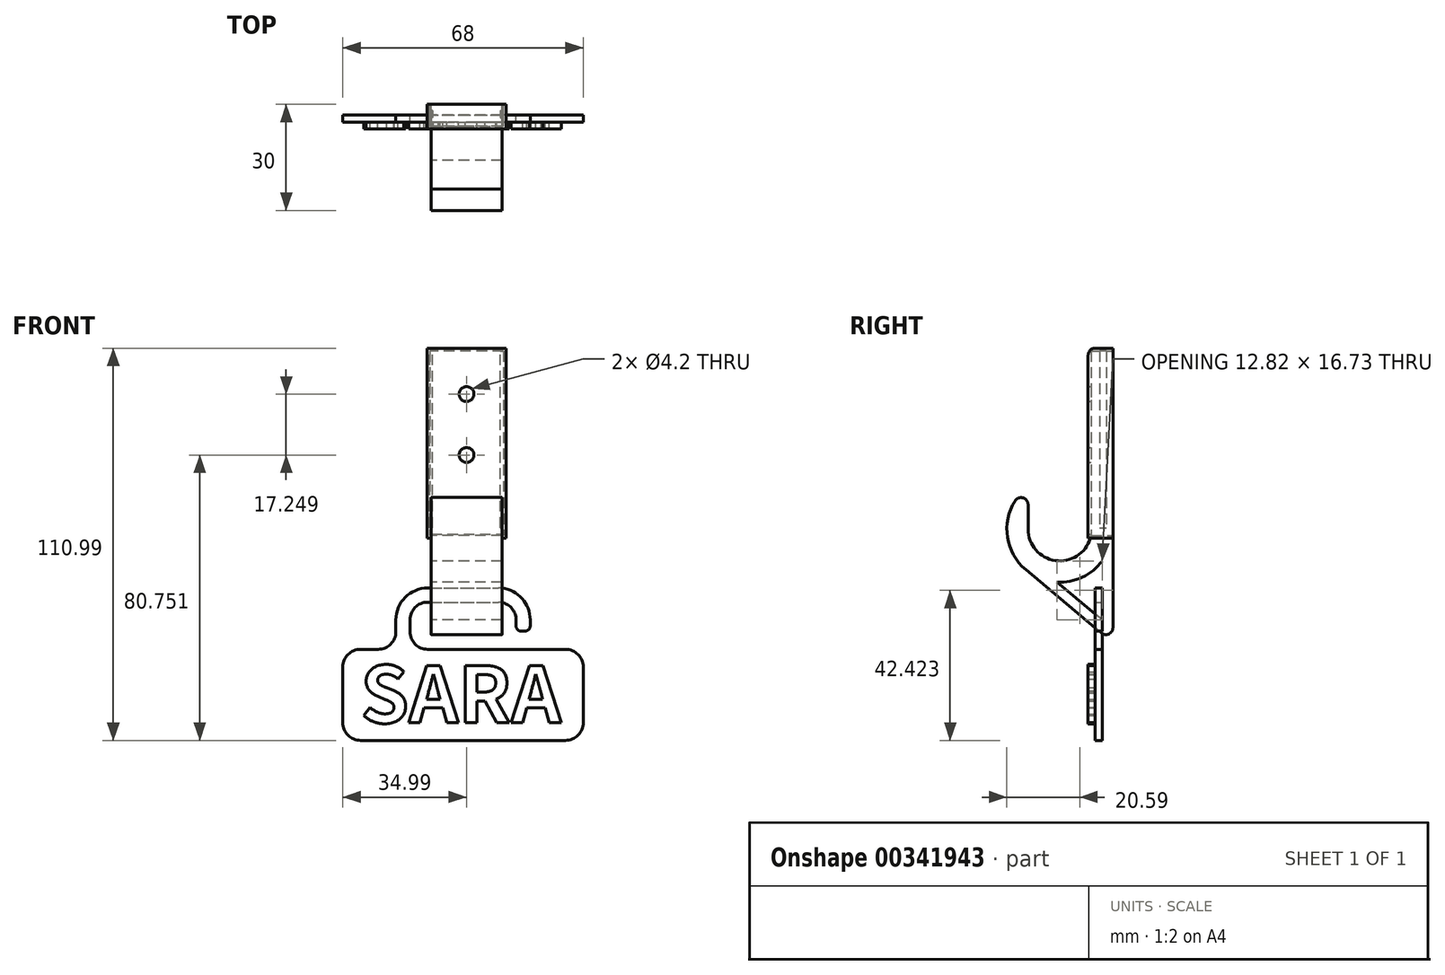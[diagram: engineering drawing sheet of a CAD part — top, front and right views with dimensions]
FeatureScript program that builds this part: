
annotation { "Feature Type Name" : "Feature", "Feature Type Description" : "" }
export const myFeature = defineFeature(function(context is Context, id is Id, definition is map)
    precondition{}
    {
        {
            var Q0;
            Q0=qCreatedBy(makeId("Right.planeOp"),FACE);
            var sketch = newSketch(context, id + "F0", { "sketchPlane" : qUnion([Q0])});
            skLineSegment(sketch, "E0.bottom", {"start": v(3, -25) * mm, "end": v(-3, -25) * mm});
            skLineSegment(sketch, "E0.top", {"start": v(3, 25) * mm, "end": v(-1, 25) * mm});
            skLineSegment(sketch, "E0.left", {"start": v(3, -25) * mm, "end": v(3, 25) * mm});
            skLineSegment(sketch, "E0.right", {"start": v(-3, -25) * mm, "end": v(-3, 23) * mm});
            skPoint(sketch, "E0.middle", {"position": v(0, 0) * mm});
            skArc(sketch, "E1", {"start": v(-24.7, -17) * mm, "mid": v(-9.28, -39.75) * mm, "end": v(-3, -13) * mm});
            skCircle(sketch, "E2", {"center": v(-12, -25) * mm, "radius": 9 * mm});
            skLineSegment(sketch, "E3", {"start": v(-21, -18.07) * mm, "end": v(-21, -25) * mm});
            skPoint(sketch, "E4.visualSharp", {"position": v(-21, -13) * mm});
            skArc(sketch, "E4.filletArc", {"start": v(-21, -18.07) * mm, "mid": v(-22.45, -16.15) * mm, "end": v(-24.7, -17) * mm});
            skLineSegment(sketch, "E5", {"start": v(3, -25) * mm, "end": v(3, -52.88) * mm});
            skLineSegment(sketch, "E6", {"start": v(-0.29, -54.41) * mm, "end": v(-21.64, -36.5) * mm});
            skPoint(sketch, "E7.visualSharp", {"position": v(3, -57.17) * mm});
            skArc(sketch, "E7.filletArc", {"start": v(-0.29, -54.41) * mm, "mid": v(1.85, -54.7) * mm, "end": v(3, -52.88) * mm});
            skPoint(sketch, "E8.visualSharp", {"position": v(-3, 25) * mm});
            skArc(sketch, "E8.filletArc", {"start": v(-1, 25) * mm, "mid": v(-2.41, 24.41) * mm, "end": v(-3, 23) * mm});
            skLineSegment(sketch, "E9.0", {"start": v(0, -50.73) * mm, "end": v(-12.82, -39.98) * mm});
            skLineSegment(sketch, "E9.1", {"start": v(0, -34) * mm, "end": v(0, -50.73) * mm});
            skSolve(sketch);
        }
        {
            var Q0;
            {var subQ1=sQuery(id+"F0.wireOp",EDGE,"E5");Q0=makeQuery(id+"F0.imprint","IMPRINT",FACE,{"disambiguationData":[TD([[makeQuery(id+"F0.imprint","IMPRINT",EDGE,{"derivedFrom":subQ1}),-1.0]])]});}
            var Q1;
            {var subQ5=sQuery(id+"F0.wireOp",EDGE,"E0.bottom");Q1=makeQuery(id+"F0.imprint","IMPRINT",FACE,{"disambiguationData":[TD([[makeQuery(id+"F0.imprint","IMPRINT",EDGE,{"derivedFrom":subQ5}),1.0]])]});}
            var Q2;
            {var subQ0=sQuery(id+"F0.wireOp",EDGE,"E0.bottom");Q2=makeQuery(id+"F0.imprint","IMPRINT",FACE,{"disambiguationData":[TD([[makeQuery(id+"F0.imprint","IMPRINT",EDGE,{"derivedFrom":subQ0}),-1.0]])]});}
            var Q3;
            Q3=makeQuery(id+"F0.imprint","IMPRINT",FACE,{"disambiguationData":[TD([[makeQuery(id+"F0.imprint","IMPRINT",EDGE,{"derivedFrom":sQuery(id+"F0.wireOp",EDGE,"E0.top")}),1.0]])]});
            extrude(context, id + "F1", {"entities" : qUnion([Q0, Q1, Q2, Q3]), "depth" : 20 * mm});
        }
        {
            var Q0;
            Q0=makeQuery(id+"F1.opExtrude","SWEPT_FACE",FACE,{"disambiguationData":[OSD([sQuery(id+"F0.wireOp",EDGE,"E0.right")])]});
            var sketch = newSketch(context, id + "F2", { "sketchPlane" : qUnion([Q0])});
            skPoint(sketch, "E10", {"position": v(10, 13.21) * mm});
            skPoint(sketch, "E10.positionSnap0", {"position": v(10, 23) * mm});
            skPoint(sketch, "E11", {"position": v(10, -4.04) * mm});
            skPoint(sketch, "E12.endSnap0", {"position": v(10, -25) * mm});
            skSolve(sketch);
        }
        {
            var Q0;
            Q0=sQuery(id+"F2.wireOp",VERTEX,"E10");
            var Q1;
            Q1=sQuery(id+"F2.wireOp",VERTEX,"E11");
            var Q2;
            Q2=makeQuery(id+"F1.opExtrude","SWEPT_BODY",BODY,{"disambiguationData":[OSD([sQuery(id+"F0.wireOp",EDGE,"E0.top"),sQuery(id+"F0.wireOp",EDGE,"E0.left"),sQuery(id+"F0.wireOp",EDGE,"E0.right"),sQuery(id+"F0.wireOp",EDGE,"E1"),sQuery(id+"F0.wireOp",EDGE,"E2"),sQuery(id+"F0.wireOp",EDGE,"E3"),sQuery(id+"F0.wireOp",EDGE,"E4.filletArc"),sQuery(id+"F0.wireOp",EDGE,"E5"),sQuery(id+"F0.wireOp",EDGE,"E6"),sQuery(id+"F0.wireOp",EDGE,"E7.filletArc"),sQuery(id+"F0.wireOp",EDGE,"E8.filletArc"),sQuery(id+"F0.wireOp",EDGE,"E9.0"),sQuery(id+"F0.wireOp",EDGE,"E9.1")])]});
            hole(context, id + "F3", {"style" : HoleStyle.C_SINK, "endStyle" : HoleEndStyle.BLIND, "standardTappedOrClearance" : lookupTablePath({ "standard" : "ISO", "engagement" : "75%", "pitch" : "0.8 mm", "size" : "M5", "type" : "Tapped" }), "standardBlindInLast" : lookupTablePath({ "standard" : "ISO", "engagement" : "75%", "pitch" : "0.8 mm", "size" : "M5", "type" : "Tapped" }), "holeDiameter" : 4.2 * mm, "cSinkDiameter" : 11.2 * mm, "cSinkAngle" : 90 * degree, "showTappedDepth" : true, "holeDepth" : 14.4 * mm, "isTappedThrough" : true, "tappedDepth" : 12 * mm, "tapClearance" : 3, "startFromSketch" : true, "locations" : qUnion([Q0, Q1]), "scope" : qUnion([Q2]), "majorDiameter" : 5 * mm});
        }
        {
            var Q0;
            Q0=makeQuery(id+"F1.opExtrude","SWEPT_FACE",FACE,{"disambiguationData":[OSD([sQuery(id+"F0.wireOp",EDGE,"E0.left"),sQuery(id+"F0.wireOp",EDGE,"E5")])]});
            var sketch = newSketch(context, id + "F4", { "sketchPlane" : qUnion([Q0])});
            skLineSegment(sketch, "E13.bottom", {"start": v(-20, 25) * mm, "end": v(0, 25) * mm});
            skLineSegment(sketch, "E13.top", {"start": v(-20, -26.42) * mm, "end": v(0, -26.42) * mm});
            skLineSegment(sketch, "E13.left", {"start": v(-20, 25) * mm, "end": v(-20, -26.42) * mm});
            skLineSegment(sketch, "E13.right", {"start": v(0, 25) * mm, "end": v(0, -26.42) * mm});
            skLineSegment(sketch, "E14.bottom", {"start": v(-21.2, 26.2) * mm, "end": v(1.2, 26.2) * mm});
            skLineSegment(sketch, "E14.top", {"start": v(-21.2, -27.62) * mm, "end": v(1.2, -27.62) * mm});
            skLineSegment(sketch, "E14.left", {"start": v(-21.2, 26.2) * mm, "end": v(-21.2, -27.62) * mm});
            skLineSegment(sketch, "E14.right", {"start": v(1.2, 26.2) * mm, "end": v(1.2, -27.62) * mm});
            skLineSegment(sketch, "E15.bottom", {"start": v(-20.4, 25.4) * mm, "end": v(0.4, 25.4) * mm});
            skLineSegment(sketch, "E15.top", {"start": v(-20.4, -26.82) * mm, "end": v(0.4, -26.82) * mm});
            skLineSegment(sketch, "E15.left", {"start": v(-20.4, 25.4) * mm, "end": v(-20.4, -26.82) * mm});
            skLineSegment(sketch, "E15.right", {"start": v(0.4, 25.4) * mm, "end": v(0.4, -26.82) * mm});
            skSolve(sketch);
        }
        {
            var Q0;
            Q0=makeQuery(id+"F4.imprint","IMPRINT",FACE,{"disambiguationData":[TD([[makeQuery(id+"F4.imprint","IMPRINT",EDGE,{"derivedFrom":sQuery(id+"F4.wireOp",EDGE,"E13.bottom")}),-1.0]])]});
            var Q1;
            Q1=makeQuery(id+"F4.imprint","IMPRINT",FACE,{"disambiguationData":[TD([[makeQuery(id+"F4.imprint","IMPRINT",EDGE,{"derivedFrom":sQuery(id+"F4.wireOp",EDGE,"E13.bottom")}),1.0]])]});
            var Q2;
            Q2=makeQuery(id+"F4.imprint","IMPRINT",FACE,{"disambiguationData":[TD([[makeQuery(id+"F4.imprint","IMPRINT",EDGE,{"derivedFrom":sQuery(id+"F4.wireOp",EDGE,"E14.bottom")}),-1.0]])]});
            var Q3;
            Q3=makeQuery(id+"F4.imprint","IMPRINT",FACE,{"disambiguationData":[TD([[makeQuery(id+"F4.imprint","IMPRINT",EDGE,{"derivedFrom":makeQuery(id+"F3.hole-0.boolean.opBoolean","INTERSECT",EDGE,{"derivedFrom":[makeQuery(id+"F1.opExtrude","SWEPT_FACE",FACE,{"disambiguationData":[OSD([sQuery(id+"F0.wireOp",EDGE,"E0.left"),sQuery(id+"F0.wireOp",EDGE,"E5")])]}),makeQuery(id+"F3.hole-0.opRevolve","SWEPT_FACE",FACE,{"disambiguationData":[OSD([sQuery(id+"F3.hole-0.sketch.wireOp",EDGE,"core_line_2")])]})]})}),-1.0]])]});
            var Q4;
            Q4=makeQuery(id+"F4.imprint","IMPRINT",FACE,{"disambiguationData":[TD([[makeQuery(id+"F4.imprint","IMPRINT",EDGE,{"derivedFrom":makeQuery(id+"F3.hole-1.boolean.opBoolean","INTERSECT",EDGE,{"derivedFrom":[makeQuery(id+"F1.opExtrude","SWEPT_FACE",FACE,{"disambiguationData":[OSD([sQuery(id+"F0.wireOp",EDGE,"E0.left"),sQuery(id+"F0.wireOp",EDGE,"E5")])]}),makeQuery(id+"F3.hole-1.opRevolve","SWEPT_FACE",FACE,{"disambiguationData":[OSD([sQuery(id+"F3.hole-1.sketch.wireOp",EDGE,"core_line_2")])]})]})}),-1.0]])]});
            extrude(context, id + "F5", {"entities" : qUnion([Q0, Q1, Q2, Q3, Q4]), "oppositeDirection" : true, "depth" : 7 * mm});
        }
        {
            var Q0;
            Q0=makeQuery(id+"F4.imprint","IMPRINT",FACE,{"disambiguationData":[TD([[makeQuery(id+"F4.imprint","IMPRINT",EDGE,{"derivedFrom":sQuery(id+"F4.wireOp",EDGE,"E13.bottom")}),-1.0]])]});
            var Q1;
            {var subQ0=sQuery(id+"F4.wireOp",EDGE,"E13.top");Q1=makeQuery(id+"F4.imprint","IMPRINT",FACE,{"disambiguationData":[TD([[makeQuery(id+"F4.imprint","IMPRINT",EDGE,{"derivedFrom":subQ0}),-1.0]])]});}
            var Q2;
            Q2=makeQuery(id+"F4.imprint","IMPRINT",FACE,{"disambiguationData":[TD([[makeQuery(id+"F4.imprint","IMPRINT",EDGE,{"derivedFrom":sQuery(id+"F4.wireOp",EDGE,"E13.bottom")}),1.0]])]});
            var Q3;
            Q3=makeQuery(id+"F4.imprint","IMPRINT",FACE,{"disambiguationData":[TD([[makeQuery(id+"F4.imprint","IMPRINT",EDGE,{"derivedFrom":makeQuery(id+"F3.hole-0.boolean.opBoolean","INTERSECT",EDGE,{"derivedFrom":[makeQuery(id+"F1.opExtrude","SWEPT_FACE",FACE,{"disambiguationData":[OSD([sQuery(id+"F0.wireOp",EDGE,"E0.left"),sQuery(id+"F0.wireOp",EDGE,"E5")])]}),makeQuery(id+"F3.hole-0.opRevolve","SWEPT_FACE",FACE,{"disambiguationData":[OSD([sQuery(id+"F3.hole-0.sketch.wireOp",EDGE,"core_line_2")])]})]})}),-1.0]])]});
            var Q4;
            Q4=makeQuery(id+"F4.imprint","IMPRINT",FACE,{"disambiguationData":[TD([[makeQuery(id+"F4.imprint","IMPRINT",EDGE,{"derivedFrom":makeQuery(id+"F3.hole-1.boolean.opBoolean","INTERSECT",EDGE,{"derivedFrom":[makeQuery(id+"F1.opExtrude","SWEPT_FACE",FACE,{"disambiguationData":[OSD([sQuery(id+"F0.wireOp",EDGE,"E0.left"),sQuery(id+"F0.wireOp",EDGE,"E5")])]}),makeQuery(id+"F3.hole-1.opRevolve","SWEPT_FACE",FACE,{"disambiguationData":[OSD([sQuery(id+"F3.hole-1.sketch.wireOp",EDGE,"core_line_2")])]})]})}),-1.0]])]});
            extrude(context, id + "F6", {"entities" : qUnion([Q0, Q1, Q2, Q3, Q4]), "operationType" : NewBodyOperationType.REMOVE, "oppositeDirection" : true, "depth" : 6.2 * mm});
        }
        {
            var Q0;
            Q0=makeQuery(id+"F5.opExtrude","CAP_EDGE",EDGE,{"disambiguationData":[OSD([sQuery(id+"F4.wireOp",EDGE,"E14.bottom")])],"isStart":false});
            fillet(context, id + "F7", {"entities" : qUnion([Q0]), "radius" : 2 * mm, "tangentPropagation" : true, "allowEdgeOverflow" : false});
        }
        {
            var Q0;
            Q0=makeQuery(id+"F6.boolean.opBoolean","COPY",FACE,{"derivedFrom":makeQuery(id+"F6.opExtrude","SWEPT_FACE",FACE,{"disambiguationData":[OSD([sQuery(id+"F4.wireOp",EDGE,"E15.bottom")])]})});
            var sketch = newSketch(context, id + "F8", { "sketchPlane" : qUnion([Q0])});
            skLineSegment(sketch, "E16.bottom", {"start": v(19.6, -1.2) * mm, "end": v(20.6, -1.2) * mm});
            skLineSegment(sketch, "E16.top", {"start": v(19.6, 0.8) * mm, "end": v(20.6, 0.8) * mm});
            skLineSegment(sketch, "E16.left", {"start": v(19.6, -1.2) * mm, "end": v(19.6, 0.8) * mm});
            skLineSegment(sketch, "E16.right", {"start": v(20.6, -1.2) * mm, "end": v(20.6, 0.8) * mm});
            skLineSegment(sketch, "E17.0", {"start": v(19.4, 1) * mm, "end": v(20.8, 1) * mm});
            skLineSegment(sketch, "E17.1", {"start": v(19.4, -1.4) * mm, "end": v(19.4, 1) * mm});
            skLineSegment(sketch, "E17.2", {"start": v(19.4, -1.4) * mm, "end": v(20.8, -1.4) * mm});
            skLineSegment(sketch, "E17.3", {"start": v(20.8, -1.4) * mm, "end": v(20.8, 1) * mm});
            skLineSegment(sketch, "E18.0.0", {"start": v(21.2, -3) * mm, "end": v(21.2, 2) * mm});
            skLineSegment(sketch, "E18.0.1", {"start": v(21.2, 2) * mm, "end": v(21.2, 4) * mm});
            skLineSegment(sketch, "E18.0.3", {"start": v(21.2, 4) * mm, "end": v(21.2, -3) * mm});
            skLineSegment(sketch, "E19.0.0", {"start": v(-0.4, -3) * mm, "end": v(0, -3) * mm});
            skLineSegment(sketch, "E19.0.2", {"start": v(0, -3) * mm, "end": v(-1.2, -3) * mm});
            skLineSegment(sketch, "E19.0.4", {"start": v(-1.2, -3) * mm, "end": v(21.2, -3) * mm});
            skLineSegment(sketch, "E19.0.6", {"start": v(21.2, -3) * mm, "end": v(20, -3) * mm});
            skLineSegment(sketch, "E19.0.8", {"start": v(20, -3) * mm, "end": v(20.4, -3) * mm});
            skLineSegment(sketch, "E19.0.10", {"start": v(20.4, -3) * mm, "end": v(-0.4, -3) * mm});
            skLineSegment(sketch, "E20.0.0", {"start": v(-1.2, -3) * mm, "end": v(-1.2, 2) * mm});
            skLineSegment(sketch, "E20.0.1", {"start": v(-1.2, 2) * mm, "end": v(21.2, 2) * mm});
            skLineSegment(sketch, "E20.0.2", {"start": v(21.2, 2) * mm, "end": v(21.2, -3) * mm});
            skLineSegment(sketch, "E20.0.3", {"start": v(21.2, -3) * mm, "end": v(-1.2, -3) * mm});
            skLineSegment(sketch, "E21", {"start": v(10, 2) * mm, "end": v(10, -3) * mm});
            skLineSegment(sketch, "E22.MirrorCS", {"start": v(0.6, -1.4) * mm, "end": v(-0.8, -1.4) * mm});
            skLineSegment(sketch, "E23.MirrorCS", {"start": v(0.4, -1.2) * mm, "end": v(-0.6, -1.2) * mm});
            skLineSegment(sketch, "E24.MirrorCS", {"start": v(-0.8, -1.4) * mm, "end": v(-0.8, 1) * mm});
            skLineSegment(sketch, "E25.MirrorCS", {"start": v(0.4, 0.8) * mm, "end": v(-0.6, 0.8) * mm});
            skLineSegment(sketch, "E26.MirrorCS", {"start": v(0.6, 1) * mm, "end": v(-0.8, 1) * mm});
            skLineSegment(sketch, "E27.MirrorCS", {"start": v(0.6, -1.4) * mm, "end": v(0.6, 1) * mm});
            skLineSegment(sketch, "E28.MirrorCS", {"start": v(0.4, -1.2) * mm, "end": v(0.4, 0.8) * mm});
            skLineSegment(sketch, "E29.MirrorCS", {"start": v(-0.6, -1.2) * mm, "end": v(-0.6, 0.8) * mm});
            skSolve(sketch);
        }
        {
            var Q0;
            {var subQ4=sQuery(id+"F8.wireOp",EDGE,"E16.left");Q0=makeQuery(id+"F8.imprint","IMPRINT",FACE,{"disambiguationData":[TD([[makeQuery(id+"F8.imprint","IMPRINT",EDGE,{"derivedFrom":subQ4}),1.0]])]});}
            var Q1;
            {var subQ0=sQuery(id+"F8.wireOp",EDGE,"E16.left");Q1=makeQuery(id+"F8.imprint","IMPRINT",FACE,{"disambiguationData":[TD([[makeQuery(id+"F8.imprint","IMPRINT",EDGE,{"derivedFrom":subQ0}),-1.0]])]});}
            var Q2;
            {var subQ0=sQuery(id+"F8.wireOp",EDGE,"E28.MirrorCS");Q2=makeQuery(id+"F8.imprint","IMPRINT",FACE,{"disambiguationData":[TD([[makeQuery(id+"F8.imprint","IMPRINT",EDGE,{"derivedFrom":subQ0}),1.0]])]});}
            var Q3;
            {var subQ0=sQuery(id+"F8.wireOp",EDGE,"E27.MirrorCS");Q3=makeQuery(id+"F8.imprint","IMPRINT",FACE,{"disambiguationData":[TD([[makeQuery(id+"F8.imprint","IMPRINT",EDGE,{"derivedFrom":subQ0}),1.0]])]});}
            extrude(context, id + "F9", {"entities" : qUnion([Q0, Q1, Q2, Q3]), "operationType" : NewBodyOperationType.REMOVE, "depth" : 50.2 * mm});
        }
        {
            var Q0;
            {var subQ0=sQuery(id+"F8.wireOp",EDGE,"E29.MirrorCS");Q0=makeQuery(id+"F8.imprint","IMPRINT",FACE,{"disambiguationData":[TD([[makeQuery(id+"F8.imprint","IMPRINT",EDGE,{"derivedFrom":subQ0}),-1.0]])]});}
            var Q1;
            {var subQ0=sQuery(id+"F8.wireOp",EDGE,"E28.MirrorCS");Q1=makeQuery(id+"F8.imprint","IMPRINT",FACE,{"disambiguationData":[TD([[makeQuery(id+"F8.imprint","IMPRINT",EDGE,{"derivedFrom":subQ0}),1.0]])]});}
            var Q2;
            {var subQ0=sQuery(id+"F8.wireOp",EDGE,"E16.left");Q2=makeQuery(id+"F8.imprint","IMPRINT",FACE,{"disambiguationData":[TD([[makeQuery(id+"F8.imprint","IMPRINT",EDGE,{"derivedFrom":subQ0}),-1.0]])]});}
            var Q3;
            {var subQ0=sQuery(id+"F8.wireOp",EDGE,"E16.right");Q3=makeQuery(id+"F8.imprint","IMPRINT",FACE,{"disambiguationData":[TD([[makeQuery(id+"F8.imprint","IMPRINT",EDGE,{"derivedFrom":subQ0}),1.0]])]});}
            extrude(context, id + "F10", {"entities" : qUnion([Q0, Q1, Q2, Q3]), "operationType" : NewBodyOperationType.ADD, "depth" : 50 * mm});
        }
        {
            var Q0;
            Q0=qCreatedBy(makeId("Front.planeOp"),FACE);
            var sketch = newSketch(context, id + "F11", { "sketchPlane" : qUnion([Q0])});
            skLineSegment(sketch, "E30.bottom", {"start": v(-1, -41.68) * mm, "end": v(19, -41.68) * mm});
            skLineSegment(sketch, "E30.top", {"start": v(-1, -45.68) * mm, "end": v(19, -45.68) * mm});
            skLineSegment(sketch, "E31.top", {"start": v(26.5, -53.88) * mm, "end": v(25.5, -53.88) * mm});
            skLineSegment(sketch, "E31.left", {"start": v(28, -50.68) * mm, "end": v(28, -52.38) * mm});
            skLineSegment(sketch, "E31.right", {"start": v(24, -50.68) * mm, "end": v(24, -52.38) * mm});
            skLineSegment(sketch, "E32.left", {"start": v(-10, -50.68) * mm, "end": v(-10, -54.03) * mm});
            skLineSegment(sketch, "E32.right", {"start": v(-6, -50.68) * mm, "end": v(-6, -54.03) * mm});
            skArc(sketch, "E33.filletArc", {"start": v(-1, -45.68) * mm, "mid": v(-4.53, -47.14) * mm, "end": v(-6, -50.68) * mm});
            skArc(sketch, "E34.filletArc", {"start": v(-1, -41.68) * mm, "mid": v(-7.36, -44.31) * mm, "end": v(-10, -50.68) * mm});
            skArc(sketch, "E35.filletArc", {"start": v(24, -50.68) * mm, "mid": v(22.54, -47.14) * mm, "end": v(19, -45.68) * mm});
            skArc(sketch, "E36.filletArc", {"start": v(28, -50.68) * mm, "mid": v(25.37, -44.31) * mm, "end": v(19, -41.68) * mm});
            skPoint(sketch, "E37.visualSharp", {"position": v(28, -53.88) * mm});
            skArc(sketch, "E37.filletArc", {"start": v(26.5, -53.88) * mm, "mid": v(27.57, -53.44) * mm, "end": v(28, -52.38) * mm});
            skPoint(sketch, "E38.visualSharp", {"position": v(24, -53.88) * mm});
            skArc(sketch, "E38.filletArc", {"start": v(24, -52.38) * mm, "mid": v(24.45, -53.44) * mm, "end": v(25.5, -53.88) * mm});
            skLineSegment(sketch, "E39.bottom", {"start": v(-1, -59.03) * mm, "end": v(38, -59.03) * mm});
            skLineSegment(sketch, "E39.top", {"start": v(-20, -84.8) * mm, "end": v(38, -84.8) * mm});
            skLineSegment(sketch, "E39.left", {"start": v(-25, -64.03) * mm, "end": v(-25, -79.8) * mm});
            skLineSegment(sketch, "E39.right", {"start": v(43, -64.03) * mm, "end": v(43, -79.8) * mm});
            skPoint(sketch, "E40.visualSharp", {"position": v(-25, -59.03) * mm});
            skArc(sketch, "E40.filletArc", {"start": v(-20, -59.03) * mm, "mid": v(-23.53, -60.5) * mm, "end": v(-25, -64.03) * mm});
            skPoint(sketch, "E41.visualSharp", {"position": v(43, -59.03) * mm});
            skArc(sketch, "E41.filletArc", {"start": v(43, -64.03) * mm, "mid": v(41.54, -60.5) * mm, "end": v(38, -59.03) * mm});
            skPoint(sketch, "E42.visualSharp", {"position": v(43, -84.8) * mm});
            skArc(sketch, "E42.filletArc", {"start": v(38, -84.8) * mm, "mid": v(41.54, -83.33) * mm, "end": v(43, -79.8) * mm});
            skPoint(sketch, "E43.visualSharp", {"position": v(-25, -84.8) * mm});
            skArc(sketch, "E43.filletArc", {"start": v(-25, -79.8) * mm, "mid": v(-23.53, -83.33) * mm, "end": v(-20, -84.8) * mm});
            skArc(sketch, "E44.filletArc", {"start": v(-6, -54.03) * mm, "mid": v(-4.53, -57.56) * mm, "end": v(-1, -59.03) * mm});
            skLineSegment(sketch, "E45", {"start": v(-20, -59.03) * mm, "end": v(-15, -59.03) * mm});
            skPoint(sketch, "E46.visualSharp", {"position": v(-10, -59.03) * mm});
            skArc(sketch, "E46.filletArc", {"start": v(-15, -59.03) * mm, "mid": v(-11.46, -57.56) * mm, "end": v(-10, -54.03) * mm});
            skText(sketch, "E47", { "text": "SARA", "fontName": "NotoSansCJKsc-Bold.otf"});
            const initialGuessF11  = {"E47": [-0.02, -0.0798, 1, 0, 0.01577]};
            skSetInitialGuess(sketch, initialGuessF11);
            skSolve(sketch);
        }
        {
            var Q0;
            Q0 = qSketchRegion(id + "F11", true);
            var Q1;
            Q1=makeQuery(id+"F11.imprint","IMPRINT",FACE,{"disambiguationData":[TD([[makeQuery(id+"F11.imprint","IMPRINT",EDGE,{"derivedFrom":sQuery(id+"F11.wireOp",EDGE,"E47.sketch_text.stroke-0")}),1.0]])]});
            var Q2;
            Q2=makeQuery(id+"F11.imprint","IMPRINT",FACE,{"disambiguationData":[TD([[makeQuery(id+"F11.imprint","IMPRINT",EDGE,{"derivedFrom":sQuery(id+"F11.wireOp",EDGE,"E47.sketch_text.stroke-16")}),1.0]])]});
            var Q3;
            Q3=makeQuery(id+"F11.imprint","IMPRINT",FACE,{"disambiguationData":[TD([[makeQuery(id+"F11.imprint","IMPRINT",EDGE,{"derivedFrom":sQuery(id+"F11.wireOp",EDGE,"E47.sketch_text.stroke-16")}),-1.0]])]});
            var Q4;
            Q4=makeQuery(id+"F11.imprint","IMPRINT",FACE,{"disambiguationData":[TD([[makeQuery(id+"F11.imprint","IMPRINT",EDGE,{"derivedFrom":sQuery(id+"F11.wireOp",EDGE,"E47.sketch_text.stroke-30")}),1.0]])]});
            var Q5;
            Q5=makeQuery(id+"F11.imprint","IMPRINT",FACE,{"disambiguationData":[TD([[makeQuery(id+"F11.imprint","IMPRINT",EDGE,{"derivedFrom":sQuery(id+"F11.wireOp",EDGE,"E47.sketch_text.stroke-30")}),-1.0]])]});
            var Q6;
            Q6=makeQuery(id+"F11.imprint","IMPRINT",FACE,{"disambiguationData":[TD([[makeQuery(id+"F11.imprint","IMPRINT",EDGE,{"derivedFrom":sQuery(id+"F11.wireOp",EDGE,"E47.sketch_text.stroke-45")}),1.0]])]});
            var Q7;
            Q7=makeQuery(id+"F11.imprint","IMPRINT",FACE,{"disambiguationData":[TD([[makeQuery(id+"F11.imprint","IMPRINT",EDGE,{"derivedFrom":sQuery(id+"F11.wireOp",EDGE,"E47.sketch_text.stroke-45")}),-1.0]])]});
            extrude(context, id + "F12", {"entities" : qUnion([Q0, Q1, Q2, Q3, Q4, Q5, Q6, Q7]), "depth" : 2 * mm});
        }
        {
            var Q0;
            Q0=makeQuery(id+"F11.imprint","IMPRINT",FACE,{"disambiguationData":[TD([[makeQuery(id+"F11.imprint","IMPRINT",EDGE,{"derivedFrom":sQuery(id+"F11.wireOp",EDGE,"E47.sketch_text.stroke-30")}),1.0]])]});
            var Q1;
            Q1=makeQuery(id+"F11.imprint","IMPRINT",FACE,{"disambiguationData":[TD([[makeQuery(id+"F11.imprint","IMPRINT",EDGE,{"derivedFrom":sQuery(id+"F11.wireOp",EDGE,"E47.sketch_text.stroke-45")}),1.0]])]});
            var Q2;
            Q2=makeQuery(id+"F11.imprint","IMPRINT",FACE,{"disambiguationData":[TD([[makeQuery(id+"F11.imprint","IMPRINT",EDGE,{"derivedFrom":sQuery(id+"F11.wireOp",EDGE,"E47.sketch_text.stroke-16")}),1.0]])]});
            var Q3;
            Q3=makeQuery(id+"F11.imprint","IMPRINT",FACE,{"disambiguationData":[TD([[makeQuery(id+"F11.imprint","IMPRINT",EDGE,{"derivedFrom":sQuery(id+"F11.wireOp",EDGE,"E47.sketch_text.stroke-0")}),1.0]])]});
            extrude(context, id + "F13", {"entities" : qUnion([Q0, Q1, Q2, Q3]), "operationType" : NewBodyOperationType.ADD, "depth" : 4 * mm});
        }
    });
